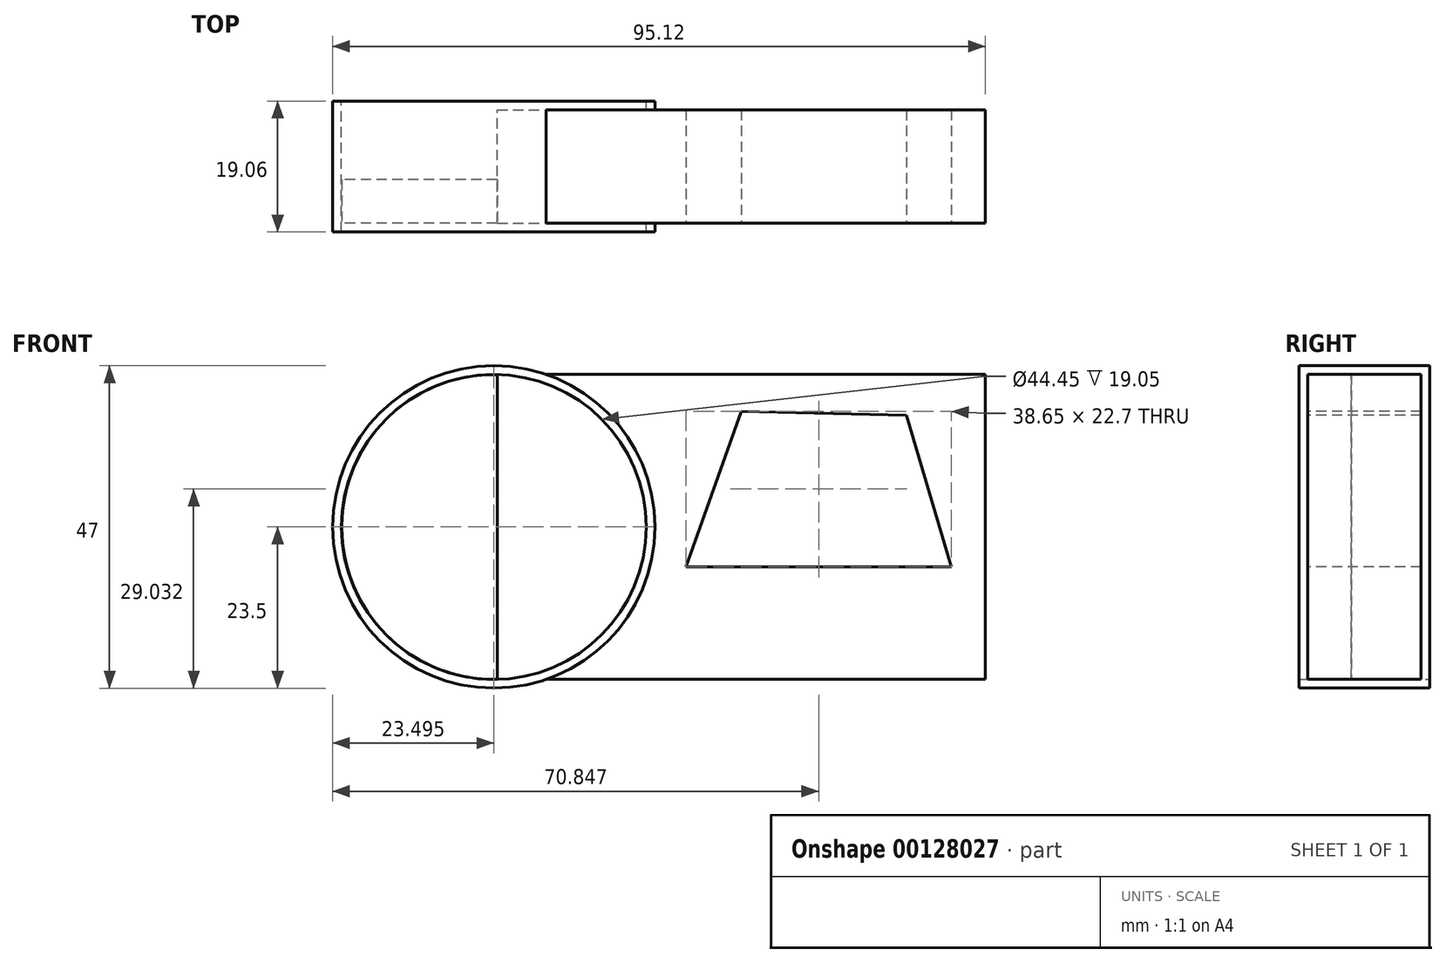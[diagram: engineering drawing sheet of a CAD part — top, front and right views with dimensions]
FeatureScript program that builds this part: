
annotation { "Feature Type Name" : "Feature", "Feature Type Description" : "" }
export const myFeature = defineFeature(function(context is Context, id is Id, definition is map)
    precondition{}
    {
        {
            var Q0;
            Q0=qCreatedBy(makeId("Front.planeOp"),FACE);
            var sketch = newSketch(context, id + "F0", { "sketchPlane" : qUnion([Q0])});
            skLineSegment(sketch, "E0.bottom", {"start": v(35.56, -22.22) * mm, "end": v(-35.56, -22.23) * mm});
            skLineSegment(sketch, "E0.top", {"start": v(35.56, 22.23) * mm, "end": v(-35.56, 22.22) * mm});
            skLineSegment(sketch, "E0.left", {"start": v(35.56, -22.22) * mm, "end": v(35.56, 22.23) * mm});
            skLineSegment(sketch, "E0.right", {"start": v(-35.56, -22.23) * mm, "end": v(-35.56, 22.22) * mm});
            skPoint(sketch, "E0.middle", {"position": v(0, 0) * mm});
            skSolve(sketch);
        }
        {
            var Q0;
            Q0=qCreatedBy(makeId("Front.planeOp"),FACE);
            var sketch = newSketch(context, id + "F1", { "sketchPlane" : qUnion([Q0])});
            skCircle(sketch, "E1", {"center": v(-36.07, 0) * mm, "radius": 23.5 * mm});
            skCircle(sketch, "E2", {"center": v(-36.07, 0) * mm, "radius": 22.23 * mm});
            skSolve(sketch);
        }
        {
            var Q0;
            Q0=makeQuery(id+"F1.imprint","IMPRINT",FACE,{"disambiguationData":[TD([[makeQuery(id+"F1.imprint","IMPRINT",EDGE,{"derivedFrom":sQuery(id+"F1.wireOp",EDGE,"E1")}),1.0]])]});
            extrude(context, id + "F2", {"entities" : qUnion([Q0]), "endBound" : BoundingType.SYMMETRIC, "depth" : 19.05 * mm});
        }
        {
            var Q0;
            Q0=makeQuery(id+"F0.imprint","IMPRINT",FACE,{"disambiguationData":[TD([[makeQuery(id+"F0.imprint","IMPRINT",EDGE,{"derivedFrom":sQuery(id+"F0.wireOp",EDGE,"E0.bottom")}),-1.0]])]});
            extrude(context, id + "F3", {"entities" : qUnion([Q0]), "operationType" : NewBodyOperationType.ADD, "endBound" : BoundingType.SYMMETRIC, "depth" : 16.5 * mm});
        }
        {
            var Q0;
            {var subQ0=sQuery(id+"F0.wireOp",EDGE,"E0.right");Q0=makeQuery(id+"F3.boolean.opBoolean","SPLIT",FACE,{"disambiguationData":[TD([makeQuery(id+"F2.opExtrude","SWEPT_FACE",FACE,{"disambiguationData":[OSD([sQuery(id+"F1.wireOp",EDGE,"E2")])]})])],"derivedFrom":makeQuery(id+"F3.opExtrude","CAP_FACE",FACE,{"disambiguationData":[OSD([sQuery(id+"F0.wireOp",EDGE,"E0.bottom"),sQuery(id+"F0.wireOp",EDGE,"E0.top"),sQuery(id+"F0.wireOp",EDGE,"E0.left"),subQ0])],"isStart":false})});}
            var sketch = newSketch(context, id + "F4", { "sketchPlane" : qUnion([Q0])});
            skArc(sketch, "E3", {"start": v(-35.56, 22.22) * mm, "mid": v(-58.24, 0) * mm, "end": v(-35.56, -22.22) * mm});
            skLineSegment(sketch, "E4", {"start": v(-35.56, -22.22) * mm, "end": v(-35.56, 22.22) * mm});
            skSolve(sketch);
        }
        {
            var Q0;
            Q0 = qSketchRegion(id + "F4", true);
            extrude(context, id + "F5", {"entities" : qUnion([Q0]), "oppositeDirection" : true, "depth" : 6.35 * mm});
        }
        {
            var Q0;
            {var subQ0=sQuery(id+"F0.wireOp",EDGE,"E0.bottom");var subQ1=sQuery(id+"F0.wireOp",EDGE,"E0.top");var subQ2=sQuery(id+"F0.wireOp",EDGE,"E0.left");Q0=makeQuery(id+"F3.boolean.opBoolean","SPLIT",FACE,{"disambiguationData":[TD([makeQuery(id+"F2.opExtrude","SWEPT_FACE",FACE,{"disambiguationData":[OSD([sQuery(id+"F1.wireOp",EDGE,"E1")])]})])],"derivedFrom":makeQuery(id+"F3.opExtrude","CAP_FACE",FACE,{"disambiguationData":[OSD([subQ0,subQ1,subQ2,sQuery(id+"F0.wireOp",EDGE,"E0.right")])],"isStart":false})});}
            var sketch = newSketch(context, id + "F6", { "sketchPlane" : qUnion([Q0])});
            skCircle(sketch, "E5.cCircle", {"center": v(11.6, 0) * mm, "radius": 20.49 * mm, "construction": true});
            skLineSegment(sketch, "E5.0", {"start": v(30.92, -6.84) * mm, "end": v(11.28, -20.33) * mm});
            skLineSegment(sketch, "E5.1", {"start": v(11.07, -20.48) * mm, "end": v(-8.04, -5.82) * mm});
            skLineSegment(sketch, "E5.2", {"start": v(-8.04, -5.82) * mm, "end": v(0, 16.88) * mm});
            skLineSegment(sketch, "E5.3", {"start": v(0, 16.88) * mm, "end": v(24.08, 16.25) * mm});
            skLineSegment(sketch, "E5.4", {"start": v(24.08, 16.25) * mm, "end": v(30.92, -6.84) * mm});
            skLineSegment(sketch, "E6", {"start": v(-8.04, -5.82) * mm, "end": v(30.61, -5.82) * mm});
            skSolve(sketch);
        }
        {
            var Q0;
            Q0=makeQuery(id+"F6.imprint","IMPRINT",FACE,{"disambiguationData":[TD([[makeQuery(id+"F6.imprint","IMPRINT",EDGE,{"derivedFrom":sQuery(id+"F6.wireOp",EDGE,"E5.2")}),-1.0]])]});
            var Q1;
            {var subQ0=sQuery(id+"F0.wireOp",EDGE,"E0.bottom");var subQ1=sQuery(id+"F0.wireOp",EDGE,"E0.top");var subQ2=sQuery(id+"F0.wireOp",EDGE,"E0.left");Q1=makeQuery(id+"F3.boolean.opBoolean","SPLIT",FACE,{"disambiguationData":[TD([makeQuery(id+"F2.opExtrude","SWEPT_FACE",FACE,{"disambiguationData":[OSD([sQuery(id+"F1.wireOp",EDGE,"E1")])]})])],"derivedFrom":makeQuery(id+"F3.opExtrude","CAP_FACE",FACE,{"disambiguationData":[OSD([subQ0,subQ1,subQ2,sQuery(id+"F0.wireOp",EDGE,"E0.right")])],"isStart":true})});}
            extrude(context, id + "F7", {"entities" : qUnion([Q0]), "operationType" : NewBodyOperationType.REMOVE, "endBound" : BoundingType.THROUGH_ALL, "oppositeDirection" : true, "endBoundEntityFace" : qUnion([Q1]), "depth" : 25.4 * mm});
        }
        {
            var Q0;
            Q0=makeQuery(id+"F6.imprint","IMPRINT",FACE,{"disambiguationData":[TD([[makeQuery(id+"F6.imprint","IMPRINT",EDGE,{"derivedFrom":sQuery(id+"F6.wireOp",EDGE,"E5.2")}),-1.0]])]});
            var sketch = newSketch(context, id + "F8", { "sketchPlane" : qUnion([Q0])});
            skLineSegment(sketch, "E7", {"start": v(0, 16.7) * mm, "end": v(30.99, -6.28) * mm});
            skLineSegment(sketch, "E8", {"start": v(-8.13, -6.28) * mm, "end": v(24.04, 15.9) * mm});
            skLineSegment(sketch, "E9", {"start": v(24.04, 15.9) * mm, "end": v(11.22, -20.17) * mm});
            skLineSegment(sketch, "E10", {"start": v(11.22, -20.17) * mm, "end": v(0, 16.7) * mm});
            skSolve(sketch);
        }
        {
            var Q0;
            Q0=sQuery(id+"F8.wireOp",EDGE,"E7");
            var Q1;
            {var subQ0=sQuery(id+"F0.wireOp",EDGE,"E0.bottom");var subQ1=sQuery(id+"F0.wireOp",EDGE,"E0.top");var subQ2=sQuery(id+"F0.wireOp",EDGE,"E0.left");Q1=makeQuery(id+"F3.boolean.opBoolean","SPLIT",FACE,{"disambiguationData":[TD([makeQuery(id+"F2.opExtrude","SWEPT_FACE",FACE,{"disambiguationData":[OSD([sQuery(id+"F1.wireOp",EDGE,"E1")])]})])],"derivedFrom":makeQuery(id+"F3.opExtrude","CAP_FACE",FACE,{"disambiguationData":[OSD([subQ0,subQ1,subQ2,sQuery(id+"F0.wireOp",EDGE,"E0.right")])],"isStart":true})});}
            extrude(context, id + "F9", {"bodyType" : ToolBodyType.SURFACE, "surfaceEntities" : qUnion([Q0]), "endBound" : BoundingType.UP_TO_SURFACE, "oppositeDirection" : true, "endBoundEntityFace" : qUnion([Q1]), "depth" : 25.4 * mm});
        }
        {
            var Q0;
            Q0=sQuery(id+"F8.wireOp",EDGE,"E8");
            var Q1;
            {var subQ0=sQuery(id+"F0.wireOp",EDGE,"E0.bottom");var subQ1=sQuery(id+"F0.wireOp",EDGE,"E0.top");var subQ2=sQuery(id+"F0.wireOp",EDGE,"E0.left");Q1=makeQuery(id+"F3.boolean.opBoolean","SPLIT",FACE,{"disambiguationData":[TD([makeQuery(id+"F2.opExtrude","SWEPT_FACE",FACE,{"disambiguationData":[OSD([sQuery(id+"F1.wireOp",EDGE,"E1")])]})])],"derivedFrom":makeQuery(id+"F3.opExtrude","CAP_FACE",FACE,{"disambiguationData":[OSD([subQ0,subQ1,subQ2,sQuery(id+"F0.wireOp",EDGE,"E0.right")])],"isStart":true})});}
            extrude(context, id + "F10", {"bodyType" : ToolBodyType.SURFACE, "surfaceEntities" : qUnion([Q0]), "endBound" : BoundingType.UP_TO_SURFACE, "oppositeDirection" : true, "endBoundEntityFace" : qUnion([Q1]), "depth" : 25.4 * mm});
        }
        {
            var Q0;
            Q0=sQuery(id+"F8.wireOp",EDGE,"E10");
            var Q1;
            {var subQ0=sQuery(id+"F0.wireOp",EDGE,"E0.bottom");var subQ1=sQuery(id+"F0.wireOp",EDGE,"E0.top");var subQ2=sQuery(id+"F0.wireOp",EDGE,"E0.left");Q1=makeQuery(id+"F3.boolean.opBoolean","SPLIT",FACE,{"disambiguationData":[TD([makeQuery(id+"F2.opExtrude","SWEPT_FACE",FACE,{"disambiguationData":[OSD([sQuery(id+"F1.wireOp",EDGE,"E1")])]})])],"derivedFrom":makeQuery(id+"F3.opExtrude","CAP_FACE",FACE,{"disambiguationData":[OSD([subQ0,subQ1,subQ2,sQuery(id+"F0.wireOp",EDGE,"E0.right")])],"isStart":true})});}
            extrude(context, id + "F11", {"bodyType" : ToolBodyType.SURFACE, "surfaceEntities" : qUnion([Q0]), "endBound" : BoundingType.UP_TO_SURFACE, "oppositeDirection" : true, "endBoundEntityFace" : qUnion([Q1]), "depth" : 25.4 * mm});
        }
        {
            var Q0;
            Q0=sQuery(id+"F8.wireOp",EDGE,"E9");
            var Q1;
            {var subQ0=sQuery(id+"F0.wireOp",EDGE,"E0.bottom");var subQ1=sQuery(id+"F0.wireOp",EDGE,"E0.top");var subQ2=sQuery(id+"F0.wireOp",EDGE,"E0.left");Q1=makeQuery(id+"F3.boolean.opBoolean","SPLIT",FACE,{"disambiguationData":[TD([makeQuery(id+"F2.opExtrude","SWEPT_FACE",FACE,{"disambiguationData":[OSD([sQuery(id+"F1.wireOp",EDGE,"E1")])]})])],"derivedFrom":makeQuery(id+"F3.opExtrude","CAP_FACE",FACE,{"disambiguationData":[OSD([subQ0,subQ1,subQ2,sQuery(id+"F0.wireOp",EDGE,"E0.right")])],"isStart":true})});}
            extrude(context, id + "F12", {"bodyType" : ToolBodyType.SURFACE, "surfaceEntities" : qUnion([Q0]), "endBound" : BoundingType.UP_TO_SURFACE, "oppositeDirection" : true, "endBoundEntityFace" : qUnion([Q1]), "depth" : 25.4 * mm});
        }
    });
